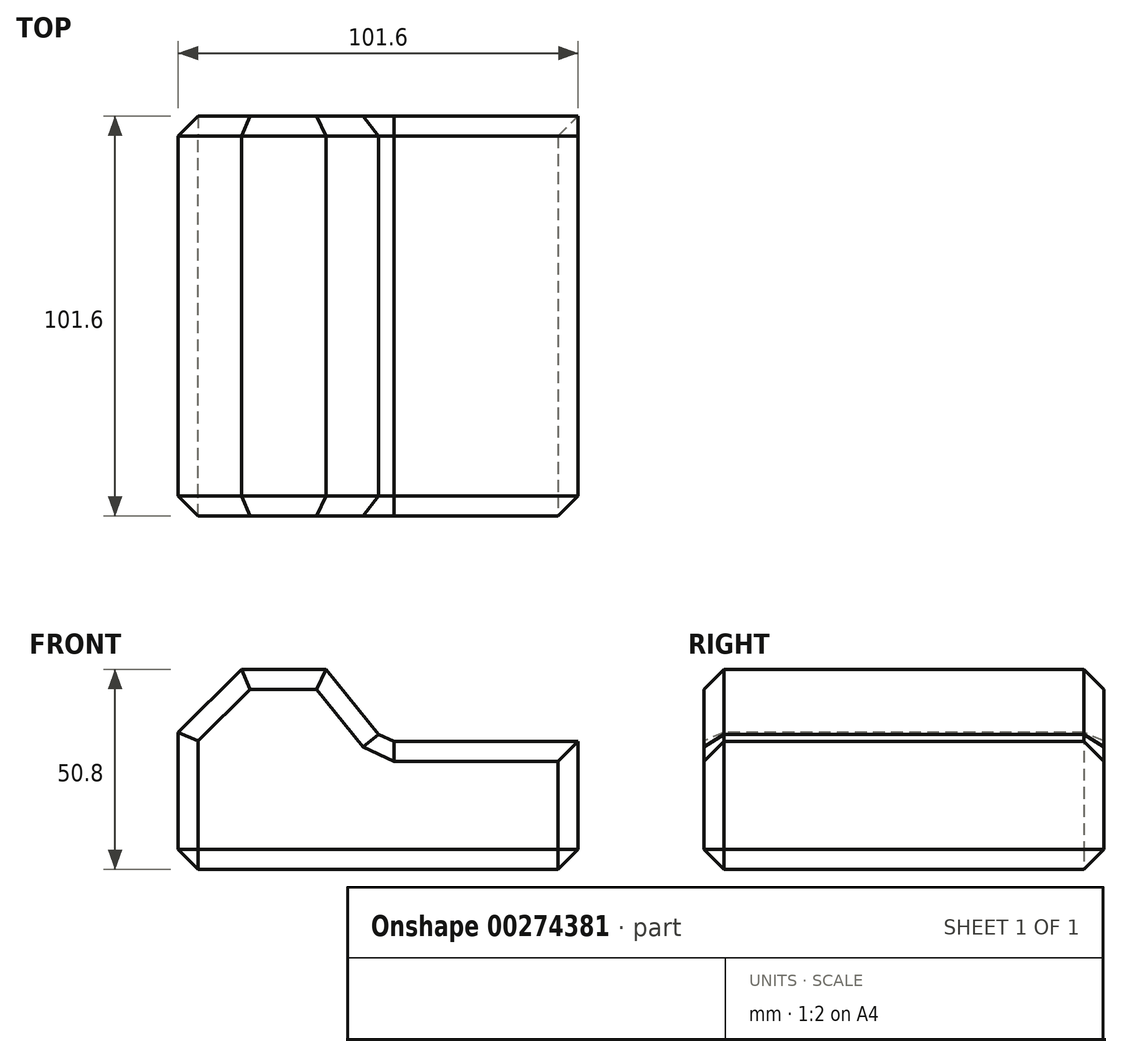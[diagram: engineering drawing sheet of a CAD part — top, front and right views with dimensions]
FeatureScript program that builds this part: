
annotation { "Feature Type Name" : "Feature", "Feature Type Description" : "" }
export const myFeature = defineFeature(function(context is Context, id is Id, definition is map)
    precondition{}
    {
        {
            var Q0;
            Q0=qCreatedBy(makeId("Top.planeOp"),FACE);
            var sketch = newSketch(context, id + "F0", { "sketchPlane" : qUnion([Q0])});
            skLineSegment(sketch, "E0.bottom", {"start": v(-52.4, 62.77) * mm, "end": v(49.2, 62.77) * mm});
            skLineSegment(sketch, "E0.top", {"start": v(-52.4, -38.83) * mm, "end": v(49.2, -38.83) * mm});
            skLineSegment(sketch, "E0.left", {"start": v(-52.4, 62.77) * mm, "end": v(-52.4, -38.83) * mm});
            skLineSegment(sketch, "E0.right", {"start": v(49.2, 62.77) * mm, "end": v(49.2, -38.83) * mm});
            skSolve(sketch);
        }
        {
            var Q0;
            Q0=makeQuery(id+"F0.imprint","IMPRINT",FACE,{"disambiguationData":[TD([[makeQuery(id+"F0.imprint","IMPRINT",EDGE,{"derivedFrom":sQuery(id+"F0.wireOp",EDGE,"E0.bottom")}),-1.0]])]});
            extrude(context, id + "F1", {"entities" : qUnion([Q0]), "depth" : 50.8 * mm});
        }
        {
            var Q0;
            Q0=makeQuery(id+"F1.opExtrude","SWEPT_FACE",FACE,{"disambiguationData":[OSD([sQuery(id+"F0.wireOp",EDGE,"E0.top")])]});
            var sketch = newSketch(context, id + "F2", { "sketchPlane" : qUnion([Q0])});
            skPoint(sketch, "E1.startSnap0", {"position": v(49.2, 25.4) * mm});
            skLineSegment(sketch, "E2", {"start": v(49.2, 32.46) * mm, "end": v(0, 32.46) * mm});
            skLineSegment(sketch, "E3", {"start": v(0, 32.46) * mm, "end": v(-14.9, 50.8) * mm});
            skLineSegment(sketch, "E4", {"start": v(-14.9, 50.8) * mm, "end": v(-36.28, 50.8) * mm});
            skLineSegment(sketch, "E5", {"start": v(-36.28, 50.8) * mm, "end": v(-52.4, 34.75) * mm});
            skSolve(sketch);
        }
        {
            var Q0;
            {var subQ0=sQuery(id+"F2.wireOp",EDGE,"E2");Q0=makeQuery(id+"F2.imprint","IMPRINT",FACE,{"disambiguationData":[TD([[makeQuery(id+"F2.imprint","IMPRINT",EDGE,{"derivedFrom":subQ0}),-1.0]])]});}
            var Q1;
            {var subQ0=sQuery(id+"F2.wireOp",EDGE,"E5");Q1=makeQuery(id+"F2.imprint","IMPRINT",FACE,{"disambiguationData":[TD([[makeQuery(id+"F2.imprint","IMPRINT",EDGE,{"derivedFrom":subQ0}),-1.0]])]});}
            extrude(context, id + "F3", {"entities" : qUnion([Q0, Q1]), "operationType" : NewBodyOperationType.REMOVE, "oppositeDirection" : true, "depth" : 116.84 * mm});
        }
        {
            var Q0;
            Q0=makeQuery(id+"F3.boolean.opBoolean","COPY",EDGE,{"derivedFrom":makeQuery(id+"F3.opExtrude","SWEPT_EDGE",EDGE,{"disambiguationData":[OSD([sQuery(id+"F0.wireOp",EDGE,"E0.top"),sQuery(id+"F2.wireOp",EDGE,"E3"),sQuery(id+"F2.wireOp",EDGE,"E4")])]})});
            var Q1;
            Q1=makeQuery(id+"F3.boolean.opBoolean","COPY",EDGE,{"derivedFrom":makeQuery(id+"F3.opExtrude","SWEPT_EDGE",EDGE,{"disambiguationData":[OSD([sQuery(id+"F2.wireOp",EDGE,"E2"),sQuery(id+"F2.wireOp",EDGE,"E3")])]})});
            var Q2;
            Q2=makeQuery(id+"F3.boolean.opBoolean","COPY",EDGE,{"derivedFrom":makeQuery(id+"F3.opExtrude","SWEPT_EDGE",EDGE,{"disambiguationData":[OSD([sQuery(id+"F0.wireOp",EDGE,"E0.top"),sQuery(id+"F0.wireOp",EDGE,"E0.right"),sQuery(id+"F2.wireOp",EDGE,"E2")])]})});
            var Q3;
            Q3=makeQuery(id+"F1.opExtrude","CAP_EDGE",EDGE,{"disambiguationData":[OSD([sQuery(id+"F0.wireOp",EDGE,"E0.right")])],"isStart":true});
            var Q4;
            Q4=makeQuery(id+"F1.opExtrude","SWEPT_EDGE",EDGE,{"disambiguationData":[OSD([sQuery(id+"F0.wireOp",EDGE,"E0.top"),sQuery(id+"F0.wireOp",EDGE,"E0.right")])]});
            var Q5;
            Q5=makeQuery(id+"F3.boolean.opBoolean","COPY",EDGE,{"derivedFrom":makeQuery(id+"F3.opExtrude","CAP_EDGE",EDGE,{"disambiguationData":[OSD([sQuery(id+"F2.wireOp",EDGE,"E2")])],"isStart":true})});
            var Q6;
            Q6=makeQuery(id+"F1.opExtrude","SWEPT_FACE",FACE,{"disambiguationData":[OSD([sQuery(id+"F0.wireOp",EDGE,"E0.top")])]});
            var Q7;
            Q7=makeQuery(id+"F3.boolean.opBoolean","COPY",EDGE,{"derivedFrom":makeQuery(id+"F3.opExtrude","SWEPT_EDGE",EDGE,{"disambiguationData":[OSD([sQuery(id+"F0.wireOp",EDGE,"E0.top"),sQuery(id+"F0.wireOp",EDGE,"E0.left"),sQuery(id+"F2.wireOp",EDGE,"E5")])]})});
            var Q8;
            Q8=makeQuery(id+"F1.opExtrude","CAP_EDGE",EDGE,{"disambiguationData":[OSD([sQuery(id+"F0.wireOp",EDGE,"E0.bottom")])],"isStart":true});
            var Q9;
            Q9=makeQuery(id+"F3.boolean.opBoolean","INTERSECT",EDGE,{"derivedFrom":[makeQuery(id+"F1.opExtrude","SWEPT_FACE",FACE,{"disambiguationData":[OSD([sQuery(id+"F0.wireOp",EDGE,"E0.bottom")])]}),makeQuery(id+"F3.opExtrude","SWEPT_FACE",FACE,{"disambiguationData":[OSD([sQuery(id+"F2.wireOp",EDGE,"E2")])]})]});
            var Q10;
            Q10=makeQuery(id+"F1.opExtrude","CAP_EDGE",EDGE,{"disambiguationData":[OSD([sQuery(id+"F0.wireOp",EDGE,"E0.bottom")])],"isStart":false});
            var Q11;
            Q11=makeQuery(id+"F3.boolean.opBoolean","INTERSECT",EDGE,{"derivedFrom":[makeQuery(id+"F1.opExtrude","SWEPT_FACE",FACE,{"disambiguationData":[OSD([sQuery(id+"F0.wireOp",EDGE,"E0.bottom")])]}),makeQuery(id+"F3.opExtrude","SWEPT_FACE",FACE,{"disambiguationData":[OSD([sQuery(id+"F2.wireOp",EDGE,"E5")])]})]});
            var Q12;
            Q12=makeQuery(id+"F1.opExtrude","SWEPT_EDGE",EDGE,{"disambiguationData":[OSD([sQuery(id+"F0.wireOp",EDGE,"E0.bottom"),sQuery(id+"F0.wireOp",EDGE,"E0.left")])]});
            var Q13;
            Q13=makeQuery(id+"F1.opExtrude","CAP_EDGE",EDGE,{"disambiguationData":[OSD([sQuery(id+"F0.wireOp",EDGE,"E0.left")])],"isStart":true});
            chamfer(context, id + "F4", {"entities" : qUnion([Q0, Q1, Q2, Q3, Q4, Q5, Q6, Q7, Q8, Q9, Q10, Q11, Q12, Q13]), "width" : 5.08 * mm, "tangentPropagation" : true});
        }
    });
